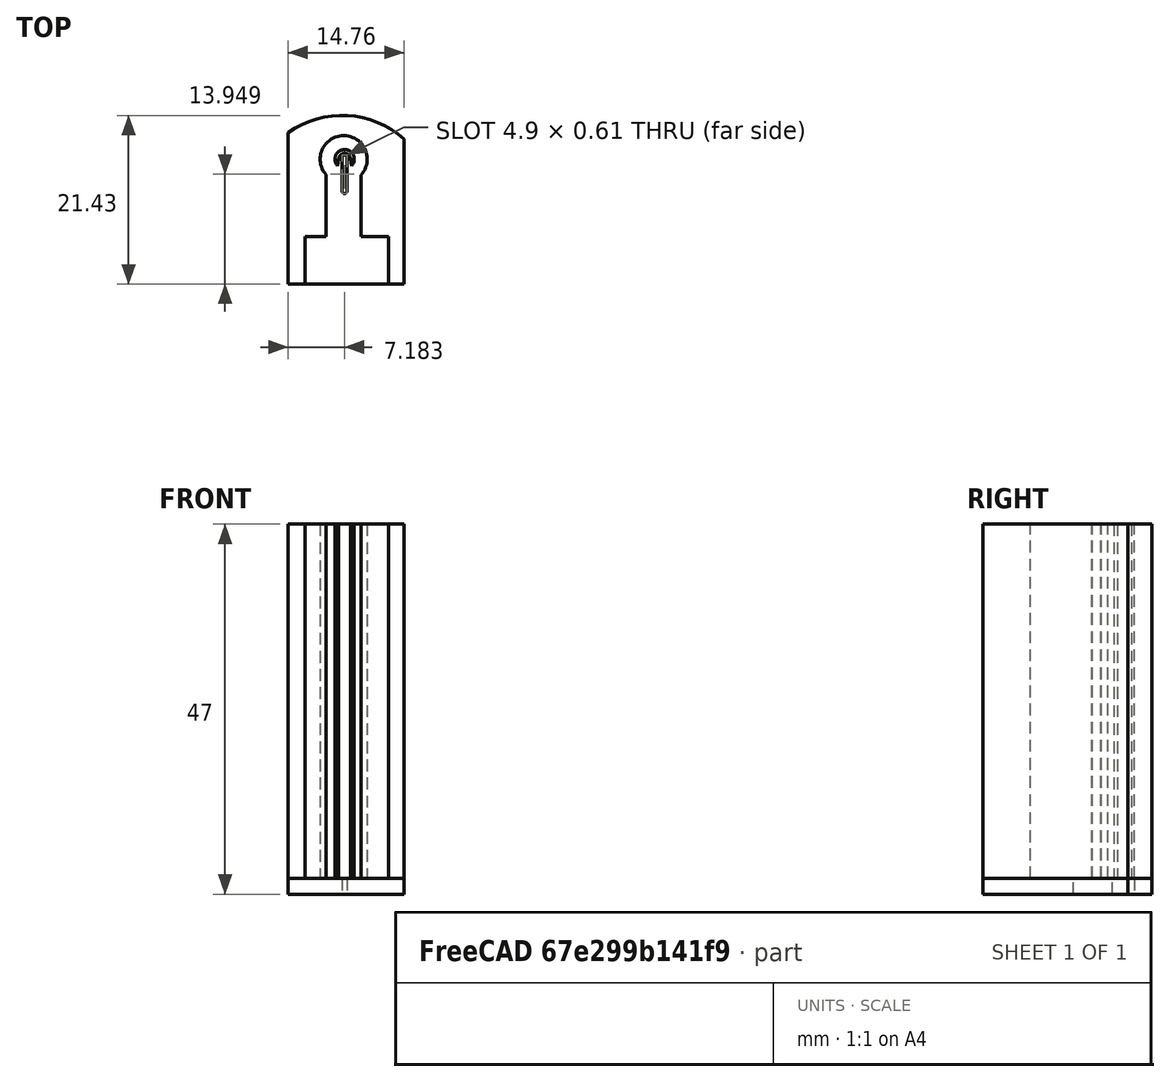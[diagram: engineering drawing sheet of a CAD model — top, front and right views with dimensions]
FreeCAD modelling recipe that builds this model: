
FCSTD DOCUMENT  (FreeCAD 0.19R24291 (Git))
Label: PotentometerPath
License: All rights reserved
LicenseURL: http://en.wikipedia.org/wiki/All_rights_reserved
objects: Sketcher::SketchObject×3, PartDesign::Pad×3, PartDesign::Body×3
note: 12 computed .brp shape members not serialized (recipe doc carries the construction recipe); baked Part::Feature solids carry a one-line shape summary decoded from their .brp

FEATURE [Sketcher::SketchObject] Sketch002
  FullyConstrained = false
  MapMode = 5
  Support = -> [XY_Plane002]
  sketch-geometry (12):
    g0: LineSegment StartX=7.19279 StartY=4.51079 StartZ=0 EndX=7.19279 EndY=23.7419 EndZ=0
    g1: ArcOfCircle CenterX=14.0463 CenterY=14.1312 CenterZ=0 NormalX=0 NormalY=0 NormalZ=1 AngleXU=0 Radius=11.8041 StartAngle=0.837045 EndAngle=2.19027
    g2: LineSegment StartX=7.19279 StartY=4.51079 StartZ=0 EndX=9.34679 EndY=4.51079 EndZ=0
    g3: LineSegment StartX=9.34679 StartY=10.5151 StartZ=0 EndX=9.34679 EndY=4.51079 EndZ=0
    g4: LineSegment StartX=19.9431 StartY=10.5151 StartZ=0 EndX=19.9431 EndY=4.51079 EndZ=0
    g5: LineSegment StartX=19.9431 StartY=4.51079 StartZ=0 EndX=21.951 EndY=4.51079 EndZ=0
    g6: LineSegment StartX=21.951 StartY=4.51079 StartZ=0 EndX=21.951 EndY=22.8977 EndZ=0
    g7: ArcOfCircle CenterX=14.255 CenterY=20.3798 CenterZ=0 NormalX=0 NormalY=0 NormalZ=1 AngleXU=0 Radius=2.99126 StartAngle=5.53784 EndAngle=10.144
    g8: LineSegment StartX=12.0046 StartY=18.4091 StartZ=0 EndX=12.0046 EndY=10.5151 EndZ=0
    g9: LineSegment StartX=16.4532 StartY=18.351 StartZ=0 EndX=16.4532 EndY=10.5151 EndZ=0
    g10: LineSegment StartX=12.0046 StartY=10.5151 StartZ=0 EndX=9.34679 EndY=10.5151 EndZ=0
    g11: LineSegment StartX=16.4532 StartY=10.5151 StartZ=0 EndX=19.9431 EndY=10.5151 EndZ=0
  constraints (22):
    c: Vertical(g0)
    c: Coincident(g1,g0)
    c: Coincident(g2,g0)
    c: Horizontal(g2)
    c: Coincident(g3,g2)
    c: Vertical(g3)
    c: Vertical(g4)
    c: Coincident(g5,g4)
    c: Horizontal(g5)
    c: Coincident(g6,g5)
    c: Coincident(g6,g1)
    c: Vertical(g6)
    c: Coincident(g8,g7)
    c: Vertical(g8)
    c: Coincident(g9,g7)
    c: Vertical(g9)
    c: Coincident(g10,g8)
    c: Coincident(g10,g3)
    c: Horizontal(g10)
    c: Coincident(g11,g9)
    c: Coincident(g11,g4)
    c: Horizontal(g11)
FEATURE [PartDesign::Pad] Pad002
  Direction = (1,1,1)
  Length = 45
  Length2 = 100
  Profile = -> Sketch002
  Type = 0
FEATURE [PartDesign::Body] Body002  label="Outside"
  Group = -> [Sketch002,Pad002]
  Origin = -> Origin002
  Tip = -> Pad002
FEATURE [Sketcher::SketchObject] Sketch003
  FullyConstrained = false
  MapMode = 5
  Support = -> [XY_Plane003]
  sketch-geometry (4):
    g0: ArcOfCircle CenterX=14.3773 CenterY=20.375 CenterZ=0 NormalX=0 NormalY=0 NormalZ=1 AngleXU=0 Radius=1.22401 StartAngle=5.49308 EndAngle=10.2047
    g1: LineSegment StartX=13.6358 StartY=20.3704 StartZ=0 EndX=13.5071 EndY=19.5142 EndZ=0
    g2: LineSegment StartX=15.1188 StartY=20.3703 StartZ=0 EndX=15.2387 EndY=19.5054 EndZ=0
    g3: ArcOfCircle CenterX=14.3773 CenterY=20.375 CenterZ=0 NormalX=0 NormalY=0 NormalZ=1 AngleXU=0 Radius=0.741531 StartAngle=6.27686 EndAngle=9.43099
  constraints (3):
    c: Coincident(g1,g0)
    c: Coincident(g2,g0)
    c: Coincident(g3,g0)
FEATURE [PartDesign::Pad] Pad003
  Direction = (0,0,-1)
  Length = 45
  Length2 = 100
  Profile = -> Sketch003
  Type = 0
FEATURE [PartDesign::Body] Body003  label="Center"
  Group = -> [Sketch003,Pad003]
  Origin = -> Origin003
  Tip = -> Pad003
FEATURE [Sketcher::SketchObject] Sketch004
  FullyConstrained = false
  MapMode = 5
  Support = -> [XY_Plane004]
  sketch-geometry (8):
    g0: LineSegment StartX=7.19279 StartY=4.51079 StartZ=0 EndX=7.19279 EndY=23.7419 EndZ=0
    g1: ArcOfCircle CenterX=14.0463 CenterY=14.1312 CenterZ=0 NormalX=0 NormalY=0 NormalZ=1 AngleXU=0 Radius=11.8041 StartAngle=0.837045 EndAngle=2.19027
    g2: LineSegment StartX=21.951 StartY=22.8977 StartZ=0 EndX=21.951 EndY=4.51079 EndZ=0
    g3: ArcOfCircle CenterX=14.3728 CenterY=16.3126 CenterZ=0 NormalX=0 NormalY=0 NormalZ=1 AngleXU=0 Radius=0.305462 StartAngle=3.14159 EndAngle=6.28319
    g4: ArcOfCircle CenterX=14.3728 CenterY=20.6055 CenterZ=0 NormalX=0 NormalY=0 NormalZ=1 AngleXU=0 Radius=0.305462 StartAngle=2e-16 EndAngle=3.14159
    g5: LineSegment StartX=14.6782 StartY=16.3126 StartZ=0 EndX=14.6782 EndY=20.6055 EndZ=0
    g6: LineSegment StartX=14.0673 StartY=16.3126 StartZ=0 EndX=14.0673 EndY=20.6055 EndZ=0
    g7: LineSegment StartX=7.19279 StartY=4.51079 StartZ=0 EndX=21.951 EndY=4.51079 EndZ=0
  constraints (13):
    c: Vertical(g0)
    c: Coincident(g1,g0)
    c: Coincident(g2,g1)
    c: Vertical(g2)
    c: Tangent(g3,g6) = 1.5708
    c: Tangent(g3,g5) = -1.5708
    c: Tangent(g5,g4) = -1.5708
    c: Tangent(g6,g4) = 1.5708
    c: Vertical(g5)
    c: Equal(g3,g4)
    c: Coincident(g7,g0)
    c: Coincident(g7,g2)
    c: Horizontal(g7)
FEATURE [PartDesign::Pad] Pad004
  Direction = (1,1,1)
  Length = 2
  Length2 = 100
  Profile = -> Sketch004
  Reversed = true
  Type = 0
FEATURE [PartDesign::Body] Body004  label="Back"
  Group = -> [Sketch004,Pad004]
  Origin = -> Origin004
  Tip = -> Pad004
